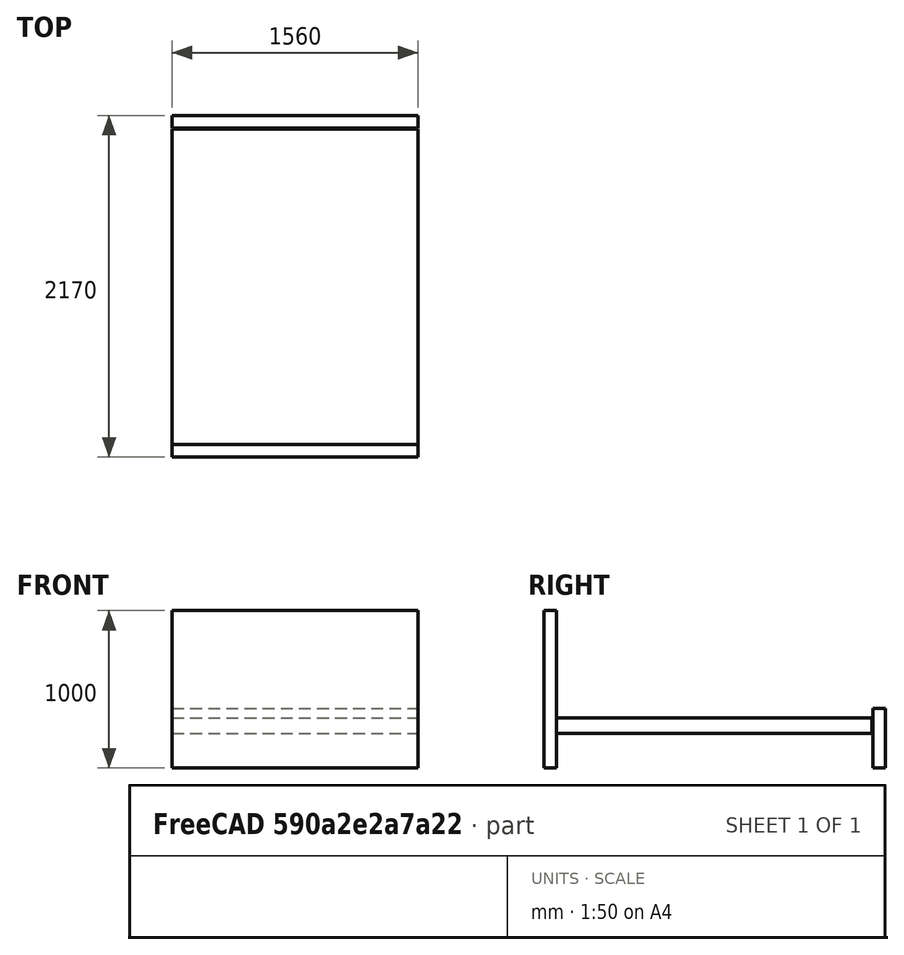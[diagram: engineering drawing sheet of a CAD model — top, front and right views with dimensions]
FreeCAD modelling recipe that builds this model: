
FCSTD DOCUMENT  (FreeCAD 1.0R38806 (Git))
Label: mueble_con_ensamblaje_y_planos
License: All rights reserved
LicenseURL: https://en.wikipedia.org/wiki/All_rights_reserved
objects: TechDraw::DrawProjGroupItem×8, Part::Box×3, Assembly::JointGroup×1, Assembly::AssemblyObject×1, TechDraw::DrawSVGTemplate×1, TechDraw::DrawProjGroup×1, TechDraw::DrawPage×1
note: 3 computed .brp shape members not serialized (recipe doc carries the construction recipe); baked Part::Feature solids carry a one-line shape summary decoded from their .brp

FEATURE [Part::Box] Box  label="cabecero"
  AttacherType = Attacher::AttachEngine3D
  Height = 1000
  Length = 1560
  Width = 80
FEATURE [Part::Box] Box001  label="pies_de_la_cama"
  AttacherType = Attacher::AttachEngine3D
  Height = 380
  Length = 1560
  Placement = pos=(0,2090,0) rot=(0,0,1;0rad)
  Width = 80
FEATURE [Part::Box] Box003  label="armadura"
  AttacherType = Attacher::AttachEngine3D
  Height = 100
  Length = 1560
  Placement = pos=(0,80,220) rot=(0,0,1;0rad)
  Width = 2004
FEATURE [Assembly::JointGroup] Joints
FEATURE [Assembly::AssemblyObject] Assembly
  Group = -> [Box,Joints,Box001,Box003]
  Origin = -> Origin
  Type = Assembly
FEATURE [TechDraw::DrawSVGTemplate] Template
  EditableTexts = approval_person=B. Hecate; creator=A. Nemesis; date_of_issue=10/17/24; document_status=In preparation; document_type=Assembly Drawing; drawing_number=DN; general_tolerances=ISO 2768-m; language_code=EN; part_material=Stainless steel Mat.No. 1.4301; responsible_department=RD; revision_index=AAA; sheet_number=1 / 1; sheet_scale=1 : 1; supplementary_title_1=ST1; supplementary_title_2=ST2; title=mueble_con_ensamblaje
  Height = 297
  Orientation = 0
  Template = <path>
  Width = 210
FEATURE [TechDraw::DrawProjGroupItem] View  label="Front"
  CoarseView = false
  Direction = (0,-1,0)
  Focus = 100
  HardHidden = false
  IsoCount = 0
  IsoHidden = false
  IsoVisible = false
  LockPosition = true
  Perspective = false
  Rotation = 0
  RotationVector = (1,0,0)
  Scale = 0.016393
  ScaleType = 2
  ScrubCount = 1
  SeamHidden = false
  SeamVisible = false
  SmoothHidden = false
  SmoothVisible = true
  Source = -> [Assembly,Origin,Box,Joints,Box001,Box003]
  Type = 0
  X = 0
  XDirection = (1,0,0)
  Y = 0
FEATURE [TechDraw::DrawProjGroupItem] ProjItem  label="FrontBottomRight"
  CoarseView = false
  Direction = (0.57735,-0.57735,-0.57735)
  Focus = 100
  HardHidden = false
  IsoCount = 0
  IsoHidden = false
  IsoVisible = false
  LockPosition = false
  Perspective = false
  Rotation = 0
  RotationVector = (1,0,0)
  Scale = 0.016393
  ScaleType = 0
  ScrubCount = 1
  SeamHidden = false
  SeamVisible = false
  SmoothHidden = false
  SmoothVisible = true
  Source = -> [Assembly,Origin,Box,Joints,Box001,Box003]
  Type = 9
  X = -49.4049
  XDirection = (0.707107,0.707107,0)
  Y = 42.3703
FEATURE [TechDraw::DrawProjGroupItem] ProjItem001  label="Bottom"
  CoarseView = false
  Direction = (0,0,-1)
  Focus = 100
  HardHidden = false
  IsoCount = 0
  IsoHidden = false
  IsoVisible = false
  LockPosition = false
  Perspective = false
  Rotation = 0
  RotationVector = (1,0,0)
  Scale = 0.016393
  ScaleType = 0
  ScrubCount = 1
  SeamHidden = false
  SeamVisible = false
  SmoothHidden = false
  SmoothVisible = true
  Source = -> [Assembly,Origin,Box,Joints,Box001,Box003]
  Type = 5
  X = 0
  XDirection = (1,0,0)
  Y = 42.3703
FEATURE [TechDraw::DrawProjGroupItem] ProjItem002  label="FrontBottomLeft"
  CoarseView = false
  Direction = (-0.57735,-0.57735,-0.57735)
  Focus = 100
  HardHidden = false
  IsoCount = 0
  IsoHidden = false
  IsoVisible = false
  LockPosition = false
  Perspective = false
  Rotation = 0
  RotationVector = (1,0,0)
  Scale = 0.016393
  ScaleType = 0
  ScrubCount = 1
  SeamHidden = false
  SeamVisible = false
  SmoothHidden = false
  SmoothVisible = true
  Source = -> [Assembly,Origin,Box,Joints,Box001,Box003]
  Type = 8
  X = 49.4049
  XDirection = (0.707107,-0.707107,0)
  Y = 42.3703
FEATURE [TechDraw::DrawProjGroupItem] ProjItem003  label="FrontTopLeft"
  CoarseView = false
  Direction = (-0.57735,-0.57735,0.57735)
  Focus = 100
  HardHidden = false
  IsoCount = 0
  IsoHidden = false
  IsoVisible = false
  LockPosition = false
  Perspective = false
  Rotation = 0
  RotationVector = (1,0,0)
  Scale = 0.016393
  ScaleType = 0
  ScrubCount = 1
  SeamHidden = false
  SeamVisible = false
  SmoothHidden = false
  SmoothVisible = true
  Source = -> [Assembly,Origin,Box,Joints,Box001,Box003]
  Type = 6
  X = 49.4049
  XDirection = (0.707107,-0.707107,0)
  Y = -38.221
FEATURE [TechDraw::DrawProjGroupItem] ProjItem004  label="Left"
  CoarseView = false
  Direction = (-1,-1e-16,0)
  Focus = 100
  HardHidden = false
  IsoCount = 0
  IsoHidden = false
  IsoVisible = false
  LockPosition = false
  Perspective = false
  Rotation = 0
  RotationVector = (1,0,0)
  Scale = 0.016393
  ScaleType = 0
  ScrubCount = 1
  SeamHidden = false
  SeamVisible = false
  SmoothHidden = false
  SmoothVisible = true
  Source = -> [Assembly,Origin,Box,Joints,Box001,Box003]
  Type = 1
  X = 49.4049
  XDirection = (1e-16,-1,0)
  Y = 0
FEATURE [TechDraw::DrawProjGroupItem] ProjItem006  label="Right"
  CoarseView = false
  Direction = (1,-1e-16,0)
  Focus = 100
  HardHidden = false
  IsoCount = 0
  IsoHidden = false
  IsoVisible = false
  LockPosition = false
  Perspective = false
  Rotation = 0
  RotationVector = (1,0,0)
  Scale = 0.016393
  ScaleType = 0
  ScrubCount = 1
  SeamHidden = false
  SeamVisible = false
  SmoothHidden = false
  SmoothVisible = true
  Source = -> [Assembly,Origin,Box,Joints,Box001,Box003]
  Type = 2
  X = -49.4049
  XDirection = (1e-16,1,0)
  Y = 0
FEATURE [TechDraw::DrawProjGroupItem] ProjItem007  label="FrontTopRight"
  CoarseView = false
  Direction = (0.57735,-0.57735,0.57735)
  Focus = 100
  HardHidden = false
  IsoCount = 0
  IsoHidden = false
  IsoVisible = false
  LockPosition = false
  Perspective = false
  Rotation = 0
  RotationVector = (1,0,0)
  Scale = 0.016393
  ScaleType = 0
  ScrubCount = 1
  SeamHidden = false
  SeamVisible = false
  SmoothHidden = false
  SmoothVisible = true
  Source = -> [Assembly,Origin,Box,Joints,Box001,Box003]
  Type = 7
  X = -49.4049
  XDirection = (0.707107,0.707107,0)
  Y = -38.221
FEATURE [TechDraw::DrawProjGroup] ProjGroup
  Anchor = -> View
  AutoDistribute = true
  LockPosition = false
  ProjectionType = 0
  Rotation = 0
  Scale = 0.016393
  ScaleType = 2
  Source = -> [Assembly,Origin,Box,Joints,Box001,Box003]
  Views = -> [View,ProjItem,ProjItem001,ProjItem002,ProjItem003,ProjItem004,ProjItem006,ProjItem007]
  X = 105
  Y = 148.5
  spacingX = 15
  spacingY = 15
FEATURE [TechDraw::DrawPage] Page
  KeepUpdated = true
  NextBalloonIndex = 1
  ProjectionType = 0
  Template = -> Template
  Views = -> [ProjGroup]
note: 1 file-system path scrubbed to <path> (originals preserved in the JSON sidecar)
